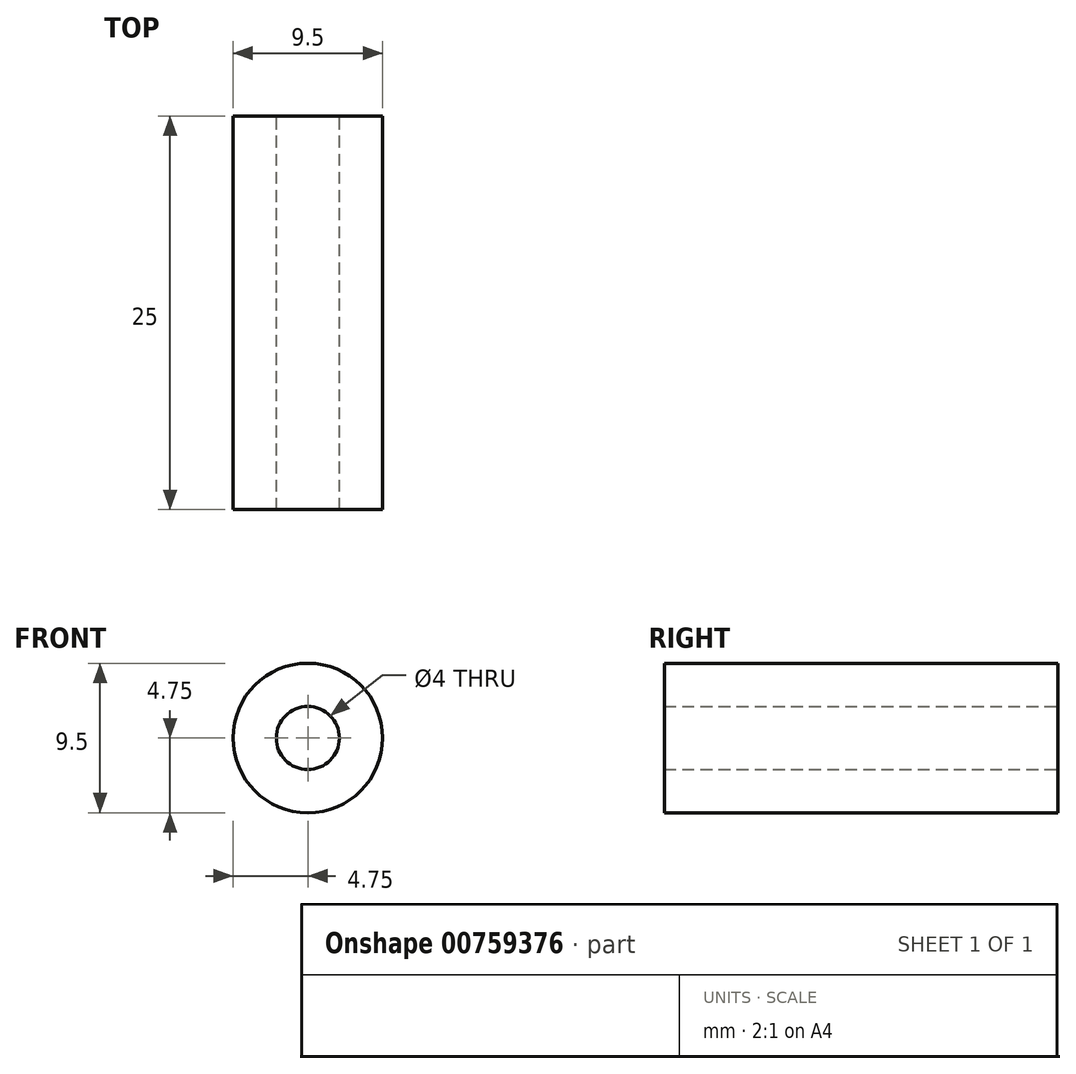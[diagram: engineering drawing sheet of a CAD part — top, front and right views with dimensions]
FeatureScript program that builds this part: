
annotation { "Feature Type Name" : "Feature", "Feature Type Description" : "" }
export const myFeature = defineFeature(function(context is Context, id is Id, definition is map)
    precondition{}
    {
        {
            var Q0;
            Q0=qCreatedBy(makeId("Front.planeOp"),FACE);
            var sketch = newSketch(context, id + "F0", { "sketchPlane" : qUnion([Q0])});
            skCircle(sketch, "E0", {"center": v(0, 0) * mm, "radius": 2 * mm});
            skCircle(sketch, "E1", {"center": v(0, 0) * mm, "radius": 4.75 * mm});
            skSolve(sketch);
        }
        {
            var Q0;
            Q0=makeQuery(id+"F0.imprint","IMPRINT",FACE,{"disambiguationData":[TD([[makeQuery(id+"F0.imprint","IMPRINT",EDGE,{"derivedFrom":sQuery(id+"F0.wireOp",EDGE,"E0")}),-1.0]])]});
            extrude(context, id + "F1", {"entities" : qUnion([Q0]), "depth" : 25 * mm, "offsetDistance" : 25 * mm});
        }
    });
